# Revit family: QF_BOURGEAT_Satellite4G_froid_2-1_vitree_ouverture_droite
name_source: partatom
category: Equipement spécialisé
revit_build: Autodesk Revit 2015 (Build: 20140606_1530(x64)
units: mm (PartAtom-declared; Revit-internal decimal feet)

## types (3) — shared parameters
Certification = NF hygiene alimentaire
Charge_gaz = 0.220 Kg
Classe Climatique = 4
Diametre_roue = 160 mm  [stored 0.524934 ft]
Dimension_verticale_vitre = 704 mm  [stored 2.30971 ft]
Fabricant = BOURGEAT
Fréquence = 50 Hz
Hauteur_roue = 200 mm  [stored 0.656168 ft]
Indice de protection = IP25
Intensité nominale = 2 A
Largeur_porte = 706 mm  [stored 2.31627 ft]
Longueur hors tout = 791 mm
Longueur_poignees_laterales = 973 mm  [stored 3.19226 ft]
Materiau_Poignee_porte = B_Elastomère_TPE_S
Materiau_bac = B_Elastomère_TPE_S
Materiau_bandage = B_Elastomère_TPE_S
Materiau_glissiere = Acrylique, transparent
Materiau_porte = Acier inoxydable, brossé
Materiau_vitre = Verre, vitrage transparent, trempé
Nature isolant = Mousse sans PU
Phase = 2
Pos_IHM_bord_gauche_porte_droite = 526 mm  [stored 1.72572 ft]
Pos_V_IHM = 98 mm  [stored 0.321522 ft]
Pos_vitre_bord_gauche_porte_droite = 103 mm  [stored 0.337927 ft]
Profondeur hors tout = 1129 mm  [stored 3.70407 ft]
Puissance frigorifique = 465 W à -5°C
Puissance électrique  = 500 W
Spécification du Fabricant = Satellite 4G
Tension = 230 V
Type Fluide Frigorigène = R134a
URL catalogue = http://www.bourgeat.fr

## per-type parameters (varying)
| type | Charge max | Consommation énergétique | Hauteur hors tout | Hauteur_poignee_porte_sol | Hauteur_poignees_laterales | Hauteur_porte | Modèle | Poids net à vide |
| GN20_tirant_droit | 200.00 kg | 3.3 Kwh/h NFD40-016 | 1166 mm | 477 mm  [stored 1.56496 ft] | 806 mm  [stored 2.64436 ft] | 919 mm | 842120 + 844000 | 120.00 kg |
| GN30_tirant_droit | 300.00 kg | 3.8 Kwh/h NFD40-016 | 1521 mm  [stored 4.99016 ft] | 564 mm | 906 mm  [stored 2.97244 ft] | 1274 mm  [stored 4.17979 ft] | 842130 + 844000 | 140.00 kg |
| GN40_tirant_droit | 300.00 kg | 4.3 Kwh/h NFD40-016 | 1876 mm | 816 mm | 906 mm  [stored 2.97244 ft] | 1629 mm  [stored 5.34449 ft] | 842140 + 844000 | 160.00 kg |

note: [stored X ft] marks values corroborated as IEEE doubles in the binary element streams (Revit-internal decimal feet)
